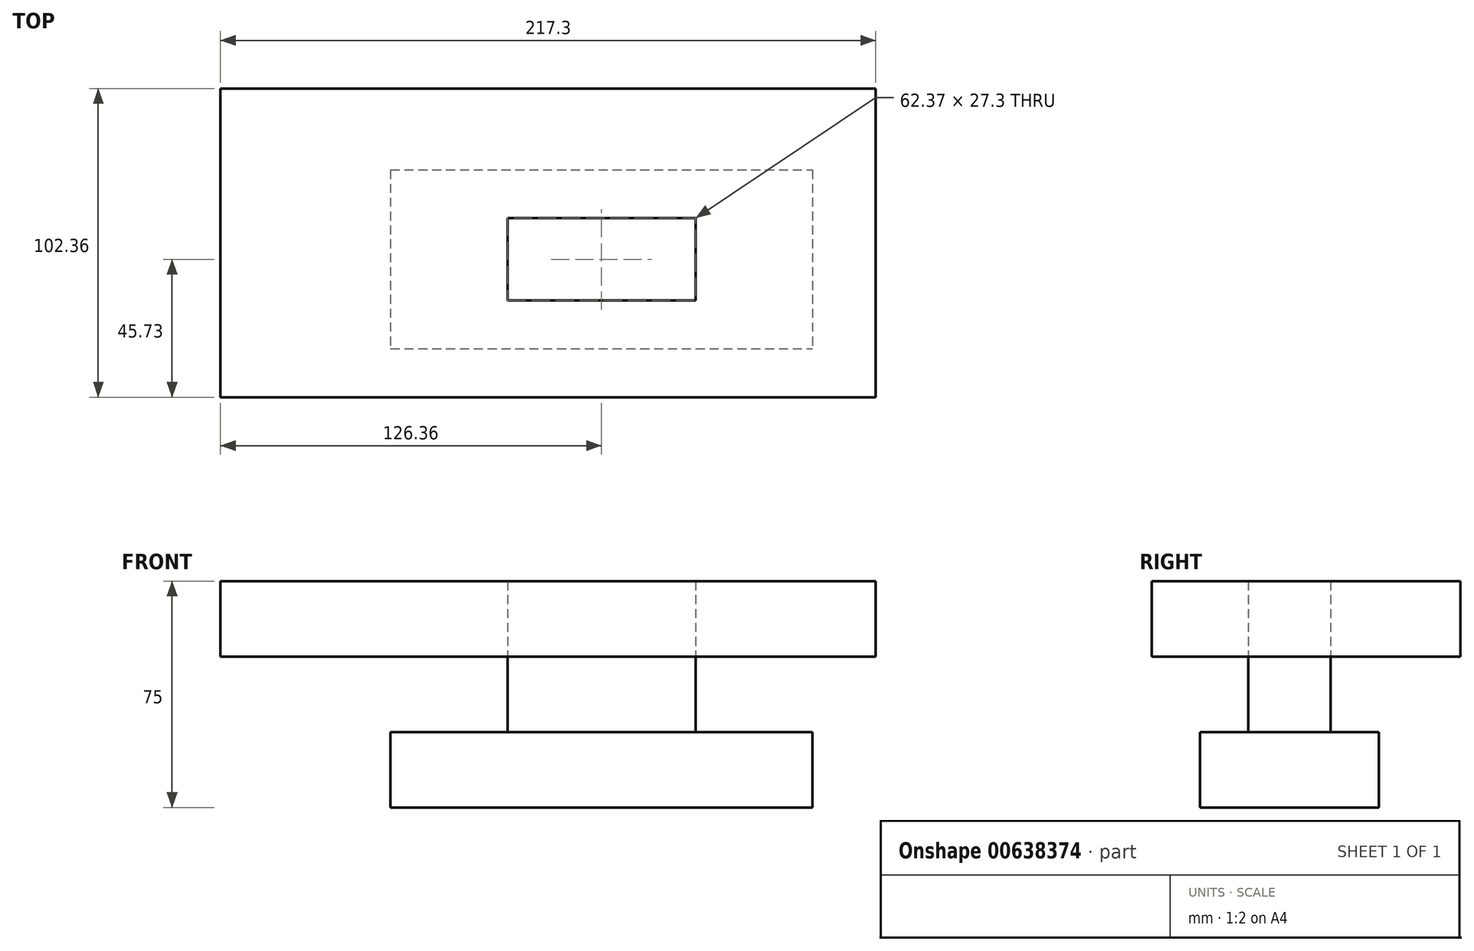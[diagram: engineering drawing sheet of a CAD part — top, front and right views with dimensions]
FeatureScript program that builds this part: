
annotation { "Feature Type Name" : "Feature", "Feature Type Description" : "" }
export const myFeature = defineFeature(function(context is Context, id is Id, definition is map)
    precondition{}
    {
        {
            var Q0;
            Q0=qCreatedBy(makeId("Top.planeOp"),FACE);
            var sketch = newSketch(context, id + "F0", { "sketchPlane" : qUnion([Q0])});
            skLineSegment(sketch, "E0.bottom", {"start": v(-69.94, 29.64) * mm, "end": v(69.94, 29.64) * mm});
            skLineSegment(sketch, "E0.top", {"start": v(-69.94, -29.64) * mm, "end": v(69.94, -29.64) * mm});
            skLineSegment(sketch, "E0.left", {"start": v(-69.94, 29.64) * mm, "end": v(-69.94, -29.64) * mm});
            skLineSegment(sketch, "E0.right", {"start": v(69.94, 29.64) * mm, "end": v(69.94, -29.64) * mm});
            skPoint(sketch, "E0.middle", {"position": v(0, 0) * mm});
            skSolve(sketch);
        }
        {
            var Q0;
            Q0=makeQuery(id+"F0.imprint","IMPRINT",FACE,{"disambiguationData":[TD([[makeQuery(id+"F0.imprint","IMPRINT",EDGE,{"derivedFrom":sQuery(id+"F0.wireOp",EDGE,"E0.bottom")}),-1.0]])]});
            extrude(context, id + "F1", {"entities" : qUnion([Q0]), "depth" : 25 * mm, "offsetDistance" : 25 * mm});
        }
        {
            var Q0;
            Q0=makeQuery(id+"F1.opExtrude","CAP_FACE",FACE,{"disambiguationData":[OSD([sQuery(id+"F0.wireOp",EDGE,"E0.bottom"),sQuery(id+"F0.wireOp",EDGE,"E0.top"),sQuery(id+"F0.wireOp",EDGE,"E0.left"),sQuery(id+"F0.wireOp",EDGE,"E0.right")])],"isStart":false});
            var sketch = newSketch(context, id + "F2", { "sketchPlane" : qUnion([Q0])});
            skLineSegment(sketch, "E1.bottom", {"start": v(-31.18, 13.65) * mm, "end": v(31.18, 13.65) * mm});
            skLineSegment(sketch, "E1.top", {"start": v(-31.18, -13.65) * mm, "end": v(31.18, -13.65) * mm});
            skLineSegment(sketch, "E1.left", {"start": v(-31.18, 13.65) * mm, "end": v(-31.18, -13.65) * mm});
            skLineSegment(sketch, "E1.right", {"start": v(31.18, 13.65) * mm, "end": v(31.18, -13.65) * mm});
            skPoint(sketch, "E1.middle", {"position": v(0, 0) * mm});
            skSolve(sketch);
        }
        {
            var Q0;
            Q0=makeQuery(id+"F2.imprint","IMPRINT",FACE,{"disambiguationData":[TD([[makeQuery(id+"F2.imprint","IMPRINT",EDGE,{"derivedFrom":sQuery(id+"F2.wireOp",EDGE,"E1.bottom")}),-1.0]])]});
            extrude(context, id + "F3", {"entities" : qUnion([Q0]), "operationType" : NewBodyOperationType.ADD, "depth" : 25 * mm, "offsetDistance" : 25 * mm});
        }
        {
            var Q0;
            Q0=makeQuery(id+"F3.opExtrude","CAP_FACE",FACE,{"disambiguationData":[OSD([sQuery(id+"F2.wireOp",EDGE,"E1.bottom"),sQuery(id+"F2.wireOp",EDGE,"E1.top"),sQuery(id+"F2.wireOp",EDGE,"E1.left"),sQuery(id+"F2.wireOp",EDGE,"E1.right")])],"isStart":false});
            var sketch = newSketch(context, id + "F4", { "sketchPlane" : qUnion([Q0])});
            skLineSegment(sketch, "E2.bottom", {"start": v(-126.36, -45.73) * mm, "end": v(90.94, -45.73) * mm});
            skLineSegment(sketch, "E2.top", {"start": v(-126.36, 56.63) * mm, "end": v(90.94, 56.63) * mm});
            skLineSegment(sketch, "E2.left", {"start": v(-126.36, -45.73) * mm, "end": v(-126.36, 56.63) * mm});
            skLineSegment(sketch, "E2.right", {"start": v(90.94, -45.73) * mm, "end": v(90.94, 56.63) * mm});
            skPoint(sketch, "E2.middle", {"position": v(-17.7, 5.45) * mm});
            skSolve(sketch);
        }
        {
            var Q0;
            Q0=makeQuery(id+"F4.imprint","IMPRINT",FACE,{"disambiguationData":[TD([[makeQuery(id+"F4.imprint","IMPRINT",EDGE,{"derivedFrom":sQuery(id+"F4.wireOp",EDGE,"E2.bottom")}),1.0]])]});
            extrude(context, id + "F5", {"entities" : qUnion([Q0]), "depth" : 25 * mm, "offsetDistance" : 25 * mm});
        }
    });
